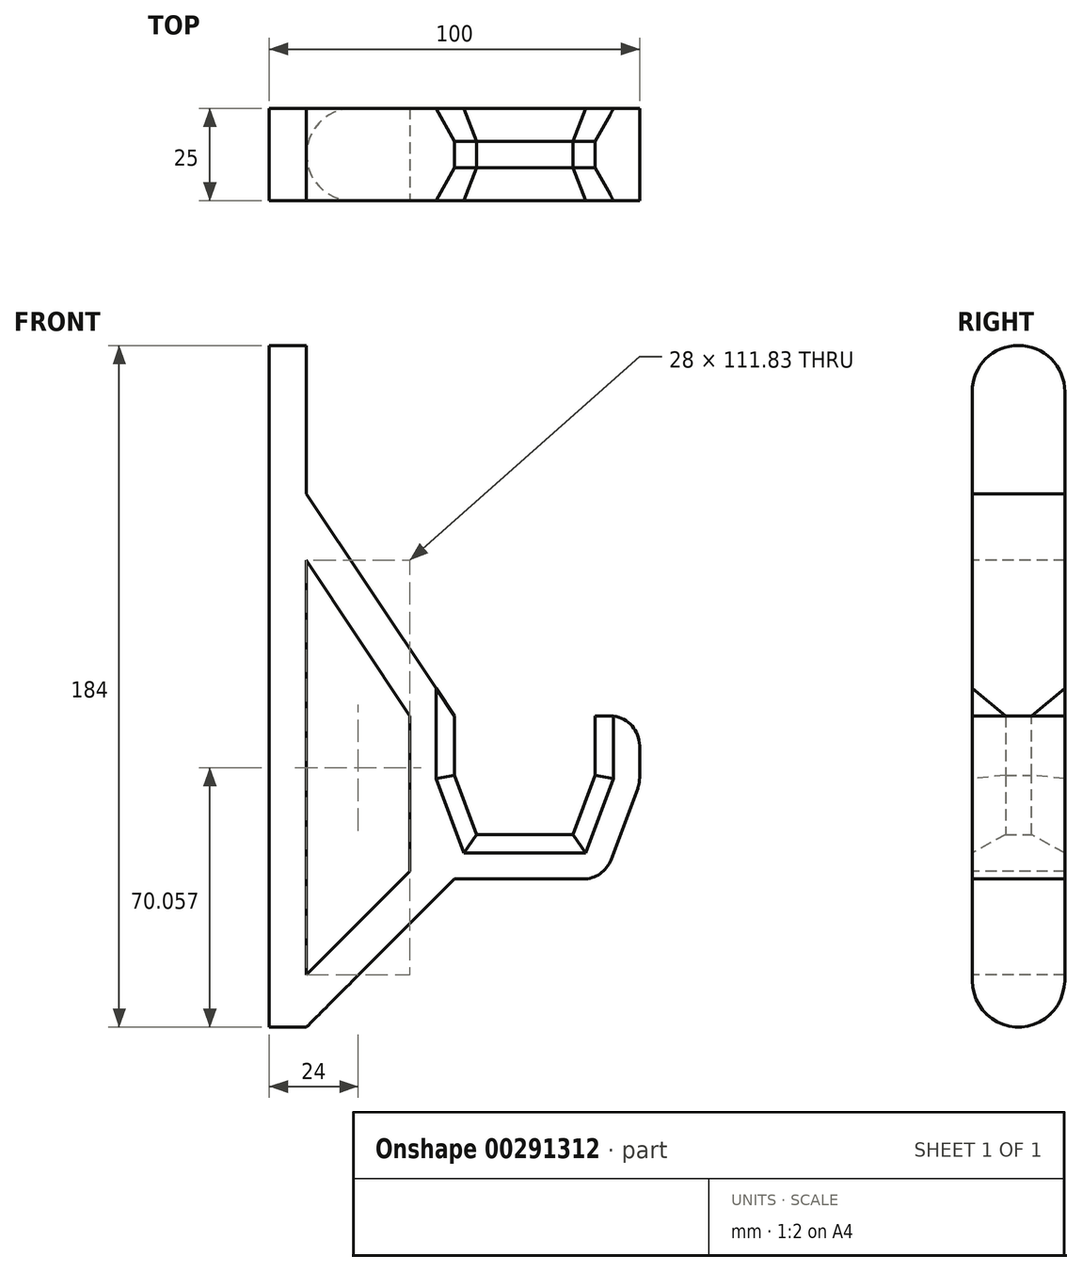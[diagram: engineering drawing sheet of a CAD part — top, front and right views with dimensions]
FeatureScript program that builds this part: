
annotation { "Feature Type Name" : "Feature", "Feature Type Description" : "" }
export const myFeature = defineFeature(function(context is Context, id is Id, definition is map)
    precondition{}
    {
        {
            var Q0;
            Q0=qCreatedBy(makeId("Front.planeOp"),FACE);
            var sketch = newSketch(context, id + "F0", { "sketchPlane" : qUnion([Q0])});
            skLineSegment(sketch, "E0", {"start": v(0, 0) * mm, "end": v(0, -16) * mm});
            skLineSegment(sketch, "E1", {"start": v(0, -16) * mm, "end": v(6, -32) * mm});
            skLineSegment(sketch, "E2", {"start": v(6, -32) * mm, "end": v(32, -32) * mm});
            skLineSegment(sketch, "E3", {"start": v(32, -32) * mm, "end": v(38, -16) * mm});
            skLineSegment(sketch, "E4", {"start": v(38, -16) * mm, "end": v(38, 0) * mm});
            skLineSegment(sketch, "E5", {"start": v(0, 0) * mm, "end": v(38, 0) * mm, "construction": true});
            skLineSegment(sketch, "E6", {"start": v(19, 0) * mm, "end": v(19, -32) * mm, "construction": true});
            skLineSegment(sketch, "E7.0", {"start": v(50, -18.18) * mm, "end": v(50, 0) * mm});
            skLineSegment(sketch, "E7.3", {"start": v(-40, -44) * mm, "end": v(40.32, -44) * mm});
            skLineSegment(sketch, "E7.4", {"start": v(40.32, -44) * mm, "end": v(50, -18.18) * mm});
            skLineSegment(sketch, "E8", {"start": v(38, 0) * mm, "end": v(50, 0) * mm});
            skLineSegment(sketch, "E9", {"start": v(-40, -44) * mm, "end": v(-40, -84) * mm});
            skLineSegment(sketch, "E10", {"start": v(-40, -84) * mm, "end": v(-50, -84) * mm});
            skLineSegment(sketch, "E11", {"start": v(-50, -84) * mm, "end": v(-50, 100) * mm});
            skLineSegment(sketch, "E12", {"start": v(-50, 100) * mm, "end": v(-40, 100) * mm});
            skLineSegment(sketch, "E13", {"start": v(-40, 100) * mm, "end": v(-40, 0) * mm});
            skLineSegment(sketch, "E14", {"start": v(-40, 0) * mm, "end": v(0, 0) * mm});
            skSolve(sketch);
        }
        {
            var Q0;
            Q0 = qSketchRegion(id + "F0", true);
            extrude(context, id + "F1", {"entities" : qUnion([Q0]), "depth" : 25 * mm});
        }
        {
            var Q0;
            Q0=makeQuery(id+"F1.opExtrude","CAP_EDGE",EDGE,{"disambiguationData":[OSD([sQuery(id+"F0.wireOp",EDGE,"E2")])],"isStart":false});
            var Q1;
            Q1=makeQuery(id+"F1.opExtrude","CAP_EDGE",EDGE,{"disambiguationData":[OSD([sQuery(id+"F0.wireOp",EDGE,"E1")])],"isStart":false});
            var Q2;
            Q2=makeQuery(id+"F1.opExtrude","CAP_EDGE",EDGE,{"disambiguationData":[OSD([sQuery(id+"F0.wireOp",EDGE,"E0")])],"isStart":false});
            var Q3;
            Q3=makeQuery(id+"F1.opExtrude","CAP_EDGE",EDGE,{"disambiguationData":[OSD([sQuery(id+"F0.wireOp",EDGE,"E3")])],"isStart":false});
            var Q4;
            Q4=makeQuery(id+"F1.opExtrude","CAP_EDGE",EDGE,{"disambiguationData":[OSD([sQuery(id+"F0.wireOp",EDGE,"E4")])],"isStart":false});
            chamfer(context, id + "F2", {"entities" : qUnion([Q0, Q1, Q2, Q3, Q4]), "chamferType" : ChamferType.TWO_OFFSETS, "width1" : 9 * mm, "oppositeDirection" : false, "width2" : 5 * mm, "tangentPropagation" : true});
        }
        {
            var Q0;
            Q0=makeQuery(id+"F1.opExtrude","CAP_EDGE",EDGE,{"disambiguationData":[OSD([sQuery(id+"F0.wireOp",EDGE,"E2")])],"isStart":true});
            var Q1;
            Q1=makeQuery(id+"F1.opExtrude","CAP_EDGE",EDGE,{"disambiguationData":[OSD([sQuery(id+"F0.wireOp",EDGE,"E1")])],"isStart":true});
            var Q2;
            Q2=makeQuery(id+"F1.opExtrude","CAP_EDGE",EDGE,{"disambiguationData":[OSD([sQuery(id+"F0.wireOp",EDGE,"E0")])],"isStart":true});
            var Q3;
            Q3=makeQuery(id+"F1.opExtrude","CAP_EDGE",EDGE,{"disambiguationData":[OSD([sQuery(id+"F0.wireOp",EDGE,"E3")])],"isStart":true});
            var Q4;
            Q4=makeQuery(id+"F1.opExtrude","CAP_EDGE",EDGE,{"disambiguationData":[OSD([sQuery(id+"F0.wireOp",EDGE,"E4")])],"isStart":true});
            chamfer(context, id + "F3", {"entities" : qUnion([Q0, Q1, Q2, Q3, Q4]), "chamferType" : ChamferType.TWO_OFFSETS, "width1" : 5 * mm, "oppositeDirection" : false, "width2" : 9 * mm, "tangentPropagation" : true});
        }
        {
            var Q0;
            Q0=makeQuery(id+"F1.opExtrude","SWEPT_EDGE",EDGE,{"disambiguationData":[OSD([sQuery(id+"F0.wireOp",EDGE,"E7.3"),sQuery(id+"F0.wireOp",EDGE,"E7.4")])]});
            var Q1;
            Q1=makeQuery(id+"F1.opExtrude","SWEPT_EDGE",EDGE,{"disambiguationData":[OSD([sQuery(id+"F0.wireOp",EDGE,"E7.0"),sQuery(id+"F0.wireOp",EDGE,"E7.4")])]});
            var Q2;
            Q2=makeQuery(id+"F1.opExtrude","SWEPT_EDGE",EDGE,{"disambiguationData":[OSD([sQuery(id+"F0.wireOp",EDGE,"E7.0"),sQuery(id+"F0.wireOp",EDGE,"E8")])]});
            fillet(context, id + "F4", {"entities" : qUnion([Q0, Q1, Q2]), "radius" : 8 * mm, "tangentPropagation" : true, "allowEdgeOverflow" : false});
        }
        {
            var Q0;
            Q0=makeQuery(id+"F1.opExtrude","CAP_EDGE",EDGE,{"disambiguationData":[OSD([sQuery(id+"F0.wireOp",EDGE,"E10")])],"isStart":false});
            var Q1;
            Q1=makeQuery(id+"F1.opExtrude","CAP_EDGE",EDGE,{"disambiguationData":[OSD([sQuery(id+"F0.wireOp",EDGE,"E10")])],"isStart":true});
            var Q2;
            Q2=makeQuery(id+"F1.opExtrude","CAP_EDGE",EDGE,{"disambiguationData":[OSD([sQuery(id+"F0.wireOp",EDGE,"E12")])],"isStart":false});
            var Q3;
            Q3=makeQuery(id+"F1.opExtrude","CAP_EDGE",EDGE,{"disambiguationData":[OSD([sQuery(id+"F0.wireOp",EDGE,"E12")])],"isStart":true});
            fillet(context, id + "F5", {"entities" : qUnion([Q0, Q1, Q2, Q3]), "radius" : 12.5 * mm, "tangentPropagation" : true, "allowEdgeOverflow" : false});
        }
        {
            var Q0;
            Q0=makeQuery(id+"F1.opExtrude","SWEPT_EDGE",EDGE,{"disambiguationData":[OSD([sQuery(id+"F0.wireOp",EDGE,"E13"),sQuery(id+"F0.wireOp",EDGE,"E14")])]});
            chamfer(context, id + "F6", {"entities" : qUnion([Q0]), "chamferType" : ChamferType.TWO_OFFSETS, "width1" : 60 * mm, "oppositeDirection" : false, "width2" : 40 * mm, "tangentPropagation" : true});
        }
        {
            var Q0;
            Q0=makeQuery(id+"F1.opExtrude","SWEPT_EDGE",EDGE,{"disambiguationData":[OSD([sQuery(id+"F0.wireOp",EDGE,"E7.3"),sQuery(id+"F0.wireOp",EDGE,"E9")])]});
            chamfer(context, id + "F7", {"entities" : qUnion([Q0]), "width" : 40 * mm, "tangentPropagation" : true});
        }
        {
            var Q0;
            Q0=makeQuery(id+"F1.opExtrude","CAP_FACE",FACE,{"disambiguationData":[OSD([sQuery(id+"F0.wireOp",EDGE,"E0"),sQuery(id+"F0.wireOp",EDGE,"E1"),sQuery(id+"F0.wireOp",EDGE,"E2"),sQuery(id+"F0.wireOp",EDGE,"E3"),sQuery(id+"F0.wireOp",EDGE,"E4"),sQuery(id+"F0.wireOp",EDGE,"E7.0"),sQuery(id+"F0.wireOp",EDGE,"E7.3"),sQuery(id+"F0.wireOp",EDGE,"E7.4"),sQuery(id+"F0.wireOp",EDGE,"E8"),sQuery(id+"F0.wireOp",EDGE,"E9"),sQuery(id+"F0.wireOp",EDGE,"E10"),sQuery(id+"F0.wireOp",EDGE,"E11"),sQuery(id+"F0.wireOp",EDGE,"E12"),sQuery(id+"F0.wireOp",EDGE,"E13"),sQuery(id+"F0.wireOp",EDGE,"E14")])],"isStart":false});
            var sketch = newSketch(context, id + "F8", { "sketchPlane" : qUnion([Q0])});
            skLineSegment(sketch, "E15", {"start": v(-40, 41.97) * mm, "end": v(-40, -69.86) * mm});
            skLineSegment(sketch, "E16", {"start": v(-40, -69.86) * mm, "end": v(-12, -41.86) * mm});
            skLineSegment(sketch, "E17", {"start": v(-12, -41.86) * mm, "end": v(-12, -0.03) * mm});
            skLineSegment(sketch, "E18", {"start": v(-12, -0.03) * mm, "end": v(-40, 41.97) * mm});
            skSolve(sketch);
        }
        {
            var Q0;
            Q0 = qSketchRegion(id + "F8", true);
            extrude(context, id + "F9", {"entities" : qUnion([Q0]), "operationType" : NewBodyOperationType.REMOVE, "endBound" : BoundingType.THROUGH_ALL, "oppositeDirection" : true, "depth" : 25 * mm});
        }
    });
